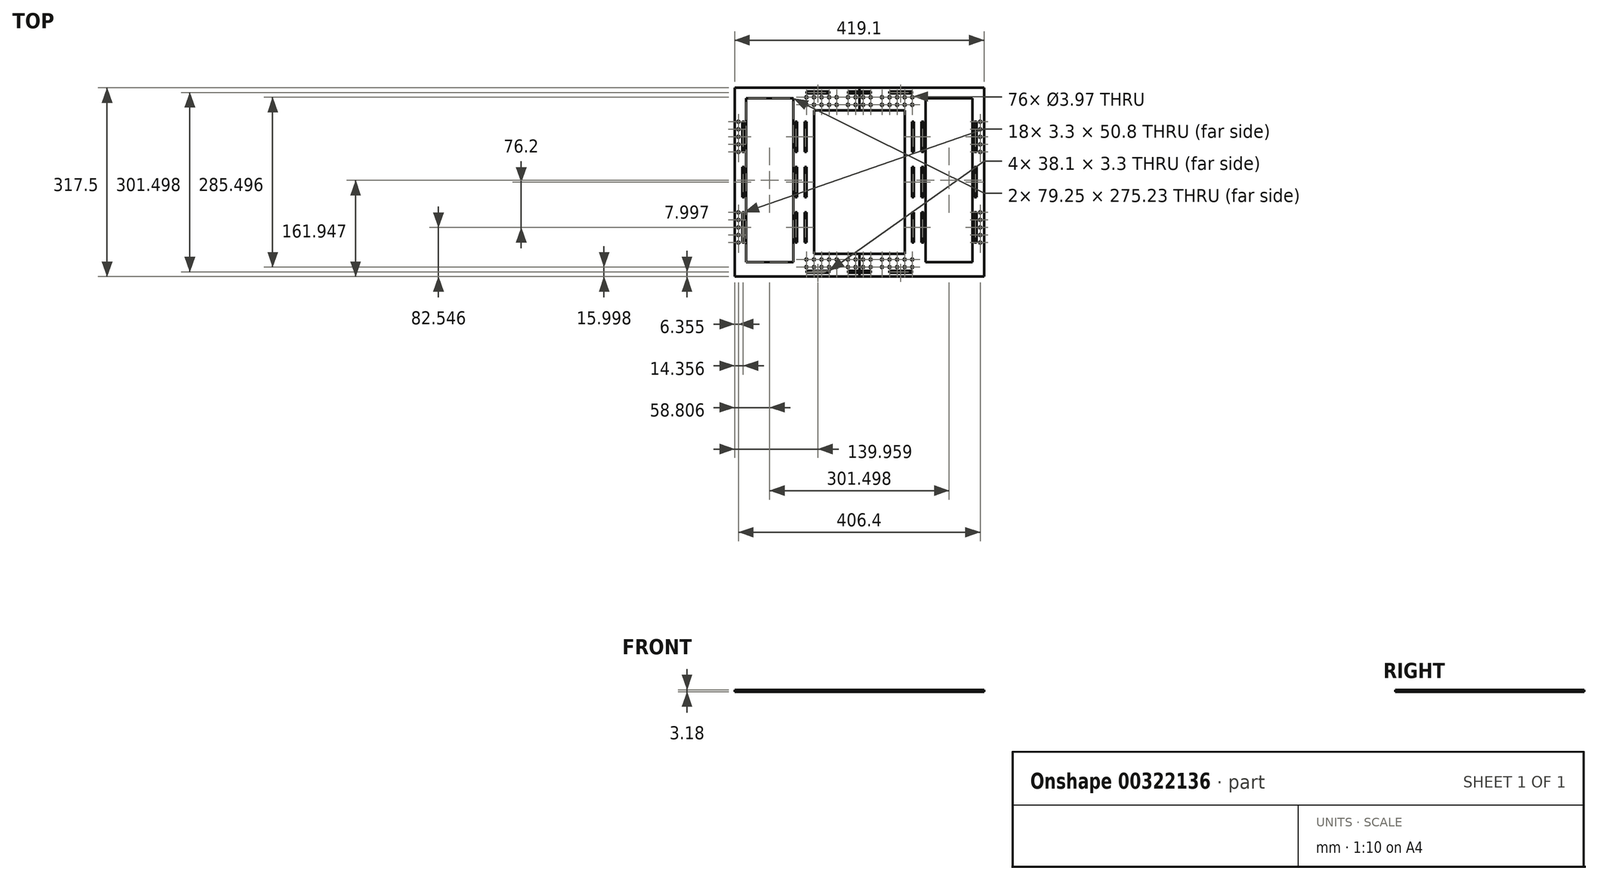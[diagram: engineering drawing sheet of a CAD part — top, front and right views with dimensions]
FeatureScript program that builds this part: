
annotation { "Feature Type Name" : "Feature", "Feature Type Description" : "" }
export const myFeature = defineFeature(function(context is Context, id is Id, definition is map)
    precondition{}
    {
        {
            var Q0;
            Q0=qCreatedBy(makeId("Top.planeOp"),FACE);
            var sketch = newSketch(context, id + "F0", { "sketchPlane" : qUnion([Q0])});
            skCircle(sketch, "E0", {"center": v(-72.78, -151.2) * mm, "radius": 1.98 * mm});
            skCircle(sketch, "E1", {"center": v(-60.08, -151.2) * mm, "radius": 1.98 * mm});
            skCircle(sketch, "E2", {"center": v(-47.38, -151.2) * mm, "radius": 1.98 * mm});
            skCircle(sketch, "E3", {"center": v(-34.68, -151.2) * mm, "radius": 1.98 * mm});
            skCircle(sketch, "E4", {"center": v(-85.48, -151.2) * mm, "radius": 1.98 * mm});
            skCircle(sketch, "E5", {"center": v(41.52, -151.2) * mm, "radius": 1.98 * mm});
            skCircle(sketch, "E6", {"center": v(54.22, -151.2) * mm, "radius": 1.98 * mm});
            skCircle(sketch, "E7", {"center": v(66.92, -151.2) * mm, "radius": 1.98 * mm});
            skCircle(sketch, "E8", {"center": v(79.62, -151.2) * mm, "radius": 1.98 * mm});
            skCircle(sketch, "E9", {"center": v(92.32, -151.2) * mm, "radius": 1.98 * mm});
            skCircle(sketch, "E10.MirrorC", {"center": v(-47.38, 134.3) * mm, "radius": 1.98 * mm});
            skCircle(sketch, "E11.MirrorC", {"center": v(-60.08, 134.3) * mm, "radius": 1.98 * mm});
            skCircle(sketch, "E12.MirrorC", {"center": v(92.32, 134.3) * mm, "radius": 1.98 * mm});
            skCircle(sketch, "E13.MirrorC", {"center": v(-34.68, 134.3) * mm, "radius": 1.98 * mm});
            skCircle(sketch, "E14.MirrorC", {"center": v(-72.78, 134.3) * mm, "radius": 1.98 * mm});
            skCircle(sketch, "E15.MirrorC", {"center": v(-85.48, 134.3) * mm, "radius": 1.98 * mm});
            skCircle(sketch, "E16.MirrorC", {"center": v(54.22, 134.3) * mm, "radius": 1.98 * mm});
            skCircle(sketch, "E17.MirrorC", {"center": v(79.62, 134.3) * mm, "radius": 1.98 * mm});
            skCircle(sketch, "E18.MirrorC", {"center": v(41.52, 134.3) * mm, "radius": 1.98 * mm});
            skCircle(sketch, "E19.MirrorC", {"center": v(66.92, 134.3) * mm, "radius": 1.98 * mm});
            skLineSegment(sketch, "E20.1.0.1", {"start": v(-193.43, 93.16) * mm, "end": v(-193.43, 42.36) * mm});
            skLineSegment(sketch, "E20.1.0.2", {"start": v(-193.43, -59.24) * mm, "end": v(-193.43, -110.04) * mm});
            skLineSegment(sketch, "E20.1.0.4", {"start": v(-193.43, 42.36) * mm, "end": v(-193.43, -33.84) * mm, "construction": true});
            skLineSegment(sketch, "E20.1.0.6", {"start": v(-190.12, -59.24) * mm, "end": v(-190.12, -110.04) * mm});
            skLineSegment(sketch, "E20.1.0.7", {"start": v(-190.12, 16.96) * mm, "end": v(-190.12, -33.84) * mm});
            skLineSegment(sketch, "E20.1.0.9", {"start": v(-186.95, 132.37) * mm, "end": v(-186.95, -142.86) * mm});
            skLineSegment(sketch, "E20.1.0.11", {"start": v(-190.12, 93.16) * mm, "end": v(-190.12, 42.36) * mm});
            skLineSegment(sketch, "E20.1.0.12", {"start": v(-193.43, 16.96) * mm, "end": v(-193.43, -33.84) * mm});
            skLineSegment(sketch, "E20.1.0.14", {"start": v(-193.43, 93.16) * mm, "end": v(-190.12, 93.16) * mm});
            skLineSegment(sketch, "E20.1.0.15", {"start": v(-193.43, -59.24) * mm, "end": v(-190.12, -59.24) * mm});
            skLineSegment(sketch, "E20.1.0.16", {"start": v(-193.43, -110.04) * mm, "end": v(-190.12, -110.04) * mm});
            skLineSegment(sketch, "E20.1.0.17", {"start": v(-193.43, 16.96) * mm, "end": v(-190.12, 16.96) * mm});
            skLineSegment(sketch, "E20.1.0.18", {"start": v(-193.43, 42.36) * mm, "end": v(-190.12, 42.36) * mm});
            skLineSegment(sketch, "E20.1.0.19", {"start": v(-193.43, -33.84) * mm, "end": v(-190.12, -33.84) * mm});
            skLineSegment(sketch, "E21", {"start": v(-206.13, 150.3) * mm, "end": v(-206.13, -167.2) * mm});
            skLineSegment(sketch, "E22.MirrorCS", {"start": v(200.27, -33.84) * mm, "end": v(196.97, -33.84) * mm});
            skLineSegment(sketch, "E23.MirrorCS", {"start": v(200.27, 42.36) * mm, "end": v(196.97, 42.36) * mm});
            skLineSegment(sketch, "E24.MirrorCS", {"start": v(200.27, 93.16) * mm, "end": v(196.97, 93.16) * mm});
            skLineSegment(sketch, "E25.MirrorCS", {"start": v(200.27, -110.04) * mm, "end": v(196.97, -110.04) * mm});
            skLineSegment(sketch, "E26.MirrorCS", {"start": v(200.27, 16.96) * mm, "end": v(196.97, 16.96) * mm});
            skLineSegment(sketch, "E27.MirrorCS", {"start": v(200.27, -59.24) * mm, "end": v(196.97, -59.24) * mm});
            skLineSegment(sketch, "E28.MirrorCS", {"start": v(200.27, 16.96) * mm, "end": v(200.27, -33.84) * mm});
            skLineSegment(sketch, "E29.MirrorCS", {"start": v(200.27, -59.24) * mm, "end": v(200.27, -110.04) * mm});
            skLineSegment(sketch, "E30.MirrorCS", {"start": v(193.8, 132.37) * mm, "end": v(193.8, -142.86) * mm});
            skLineSegment(sketch, "E31.MirrorCS", {"start": v(196.97, -59.24) * mm, "end": v(196.97, -110.04) * mm});
            skLineSegment(sketch, "E32.MirrorCS", {"start": v(200.27, 42.36) * mm, "end": v(200.27, -33.84) * mm, "construction": true});
            skLineSegment(sketch, "E33.MirrorCS", {"start": v(200.27, 93.16) * mm, "end": v(200.27, 42.36) * mm});
            skLineSegment(sketch, "E34.MirrorCS", {"start": v(196.97, 16.96) * mm, "end": v(196.97, -33.84) * mm});
            skLineSegment(sketch, "E35.MirrorCS", {"start": v(196.97, 93.16) * mm, "end": v(196.97, 42.36) * mm});
            skLineSegment(sketch, "E36.MirrorCS", {"start": v(212.97, 150.3) * mm, "end": v(212.97, -167.2) * mm});
            skCircle(sketch, "E37.MirrorC", {"center": v(-199.78, 93.16) * mm, "radius": 1.98 * mm});
            skCircle(sketch, "E38.MirrorC", {"center": v(-199.78, -71.94) * mm, "radius": 1.98 * mm});
            skCircle(sketch, "E39.MirrorC", {"center": v(-199.78, 67.76) * mm, "radius": 1.98 * mm});
            skCircle(sketch, "E40.MirrorC", {"center": v(-199.78, -84.64) * mm, "radius": 1.98 * mm});
            skCircle(sketch, "E41.MirrorC", {"center": v(-199.78, -110.04) * mm, "radius": 1.98 * mm});
            skCircle(sketch, "E42.MirrorC", {"center": v(-199.78, 80.46) * mm, "radius": 1.98 * mm});
            skCircle(sketch, "E43.MirrorC", {"center": v(-199.78, 42.36) * mm, "radius": 1.98 * mm});
            skLineSegment(sketch, "E44.MirrorCS", {"start": v(-193.43, 67.76) * mm, "end": v(-206.13, 67.76) * mm, "construction": true});
            skCircle(sketch, "E45.MirrorC", {"center": v(-199.78, -59.24) * mm, "radius": 1.98 * mm});
            skCircle(sketch, "E46.MirrorC", {"center": v(-199.78, -97.34) * mm, "radius": 1.98 * mm});
            skCircle(sketch, "E47.MirrorC", {"center": v(-199.78, 55.06) * mm, "radius": 1.98 * mm});
            skLineSegment(sketch, "E48.MirrorCS", {"start": v(-190.12, 42.36) * mm, "end": v(-206.13, 42.36) * mm, "construction": true});
            skLineSegment(sketch, "E49.MirrorCS", {"start": v(-193.43, -84.64) * mm, "end": v(-206.13, -84.64) * mm, "construction": true});
            skLineSegment(sketch, "E50.MirrorCS", {"start": v(-199.78, -84.64) * mm, "end": v(-199.78, -110.04) * mm, "construction": true});
            skLineSegment(sketch, "E51.MirrorCS", {"start": v(-199.78, 67.76) * mm, "end": v(-199.78, 93.16) * mm, "construction": true});
            skCircle(sketch, "E52.MirrorC", {"center": v(206.62, -84.64) * mm, "radius": 1.98 * mm});
            skCircle(sketch, "E53.MirrorC", {"center": v(206.62, -71.94) * mm, "radius": 1.98 * mm});
            skCircle(sketch, "E54.MirrorC", {"center": v(206.62, 93.16) * mm, "radius": 1.98 * mm});
            skCircle(sketch, "E55.MirrorC", {"center": v(206.62, 67.76) * mm, "radius": 1.98 * mm});
            skCircle(sketch, "E56.MirrorC", {"center": v(206.62, -110.04) * mm, "radius": 1.98 * mm});
            skCircle(sketch, "E57.MirrorC", {"center": v(206.62, 80.46) * mm, "radius": 1.98 * mm});
            skCircle(sketch, "E58.MirrorC", {"center": v(206.62, 55.06) * mm, "radius": 1.98 * mm});
            skCircle(sketch, "E59.MirrorC", {"center": v(206.62, 42.36) * mm, "radius": 1.98 * mm});
            skCircle(sketch, "E60.MirrorC", {"center": v(206.62, -97.34) * mm, "radius": 1.98 * mm});
            skCircle(sketch, "E61.MirrorC", {"center": v(206.62, -59.24) * mm, "radius": 1.98 * mm});
            skLineSegment(sketch, "E62.MirrorCS", {"start": v(206.62, -84.64) * mm, "end": v(206.62, -110.04) * mm, "construction": true});
            skLineSegment(sketch, "E63.MirrorCS", {"start": v(206.62, 67.76) * mm, "end": v(206.62, 93.16) * mm, "construction": true});
            skLineSegment(sketch, "E64.bottom", {"start": v(114.55, -167.2) * mm, "end": v(-107.7, -167.2) * mm});
            skLineSegment(sketch, "E64.top", {"start": v(114.55, 150.3) * mm, "end": v(-107.7, 150.3) * mm});
            skLineSegment(sketch, "E64.left", {"start": v(114.55, -167.2) * mm, "end": v(114.55, 150.3) * mm, "construction": true});
            skPoint(sketch, "E64.middle", {"position": v(3.42, -8.44) * mm});
            skLineSegment(sketch, "E65.bottom", {"start": v(-85.22, 143.96) * mm, "end": v(-47.12, 143.96) * mm});
            skLineSegment(sketch, "E65.top", {"start": v(-85.22, 140.65) * mm, "end": v(-47.12, 140.65) * mm});
            skLineSegment(sketch, "E65.left", {"start": v(-85.22, 143.96) * mm, "end": v(-85.22, 140.65) * mm});
            skLineSegment(sketch, "E65.right", {"start": v(-47.12, 143.96) * mm, "end": v(-47.12, 140.65) * mm});
            skLineSegment(sketch, "E66.bottom", {"start": v(-15.63, 143.96) * mm, "end": v(22.47, 143.96) * mm});
            skLineSegment(sketch, "E66.top", {"start": v(-15.63, 140.65) * mm, "end": v(22.47, 140.65) * mm});
            skLineSegment(sketch, "E66.left", {"start": v(-15.63, 143.96) * mm, "end": v(-15.63, 140.65) * mm});
            skLineSegment(sketch, "E66.right", {"start": v(22.47, 143.96) * mm, "end": v(22.47, 140.65) * mm});
            skLineSegment(sketch, "E67", {"start": v(-47.12, 143.96) * mm, "end": v(-15.63, 143.96) * mm, "construction": true});
            skLineSegment(sketch, "E68.MirrorCS", {"start": v(92.07, 140.65) * mm, "end": v(53.97, 140.65) * mm});
            skLineSegment(sketch, "E69.MirrorCS", {"start": v(92.07, 143.96) * mm, "end": v(53.97, 143.96) * mm});
            skLineSegment(sketch, "E70.MirrorCS", {"start": v(53.97, 143.96) * mm, "end": v(53.97, 140.65) * mm});
            skLineSegment(sketch, "E71.MirrorCS", {"start": v(92.07, 143.96) * mm, "end": v(92.07, 140.65) * mm});
            skLineSegment(sketch, "E72.MirrorCS", {"start": v(-47.12, -160.84) * mm, "end": v(-47.12, -157.54) * mm});
            skLineSegment(sketch, "E73.MirrorCS", {"start": v(-15.63, -157.54) * mm, "end": v(22.47, -157.54) * mm});
            skLineSegment(sketch, "E74.MirrorCS", {"start": v(22.47, -160.84) * mm, "end": v(22.47, -157.54) * mm});
            skLineSegment(sketch, "E75.MirrorCS", {"start": v(92.07, -157.54) * mm, "end": v(53.97, -157.54) * mm});
            skLineSegment(sketch, "E76.MirrorCS", {"start": v(53.97, -160.84) * mm, "end": v(53.97, -157.54) * mm});
            skLineSegment(sketch, "E77.MirrorCS", {"start": v(-85.22, -157.54) * mm, "end": v(-47.12, -157.54) * mm});
            skLineSegment(sketch, "E78.MirrorCS", {"start": v(92.07, -160.84) * mm, "end": v(92.07, -157.54) * mm});
            skLineSegment(sketch, "E79.MirrorCS", {"start": v(-15.63, -160.84) * mm, "end": v(-15.63, -157.54) * mm});
            skLineSegment(sketch, "E80.MirrorCS", {"start": v(92.07, -160.84) * mm, "end": v(53.97, -160.84) * mm});
            skLineSegment(sketch, "E81.MirrorCS", {"start": v(-15.63, -160.84) * mm, "end": v(22.47, -160.84) * mm});
            skLineSegment(sketch, "E82.MirrorCS", {"start": v(-47.12, -160.84) * mm, "end": v(-15.63, -160.84) * mm, "construction": true});
            skLineSegment(sketch, "E83.MirrorCS", {"start": v(-85.22, -160.84) * mm, "end": v(-47.12, -160.84) * mm});
            skLineSegment(sketch, "E84.MirrorCS", {"start": v(-85.22, -160.84) * mm, "end": v(-85.22, -157.54) * mm});
            skLineSegment(sketch, "E85.bottom", {"start": v(-104.53, 93.16) * mm, "end": v(-101.22, 93.16) * mm});
            skLineSegment(sketch, "E85.top", {"start": v(-104.53, 42.36) * mm, "end": v(-101.22, 42.36) * mm});
            skLineSegment(sketch, "E85.left", {"start": v(-104.53, 93.16) * mm, "end": v(-104.53, 42.36) * mm});
            skLineSegment(sketch, "E85.right", {"start": v(-101.22, 93.16) * mm, "end": v(-101.22, 42.36) * mm});
            skLineSegment(sketch, "E86.0.1.0", {"start": v(-101.22, 16.96) * mm, "end": v(-101.22, -33.84) * mm});
            skLineSegment(sketch, "E86.0.1.1", {"start": v(-104.53, 16.96) * mm, "end": v(-104.53, -33.84) * mm});
            skLineSegment(sketch, "E86.0.1.2", {"start": v(-104.53, 16.96) * mm, "end": v(-101.22, 16.96) * mm});
            skLineSegment(sketch, "E86.0.1.3", {"start": v(-104.53, -33.84) * mm, "end": v(-101.22, -33.84) * mm});
            skLineSegment(sketch, "E86.0.2.0", {"start": v(-101.22, -59.24) * mm, "end": v(-101.22, -110.04) * mm});
            skLineSegment(sketch, "E86.0.2.1", {"start": v(-104.53, -59.24) * mm, "end": v(-104.53, -110.04) * mm});
            skLineSegment(sketch, "E86.0.2.2", {"start": v(-104.53, -59.24) * mm, "end": v(-101.22, -59.24) * mm});
            skLineSegment(sketch, "E86.0.2.3", {"start": v(-104.53, -110.04) * mm, "end": v(-101.22, -110.04) * mm});
            skLineSegment(sketch, "E86.direction1", {"start": v(-104.53, 42.36) * mm, "end": v(-88.52, 42.36) * mm, "construction": true});
            skLineSegment(sketch, "E86.direction2", {"start": v(-104.53, 42.36) * mm, "end": v(-104.53, -33.84) * mm, "construction": true});
            skLineSegment(sketch, "E87.MirrorCS", {"start": v(108.07, 16.96) * mm, "end": v(108.07, -33.84) * mm});
            skLineSegment(sketch, "E88.MirrorCS", {"start": v(111.37, -59.24) * mm, "end": v(108.07, -59.24) * mm});
            skLineSegment(sketch, "E89.MirrorCS", {"start": v(111.37, 16.96) * mm, "end": v(111.37, -33.84) * mm});
            skLineSegment(sketch, "E90.MirrorCS", {"start": v(111.37, -110.04) * mm, "end": v(108.07, -110.04) * mm});
            skLineSegment(sketch, "E91.MirrorCS", {"start": v(111.37, 16.96) * mm, "end": v(108.07, 16.96) * mm});
            skLineSegment(sketch, "E92.MirrorCS", {"start": v(111.37, -33.84) * mm, "end": v(108.07, -33.84) * mm});
            skLineSegment(sketch, "E93.MirrorCS", {"start": v(111.37, 42.36) * mm, "end": v(111.37, -33.84) * mm, "construction": true});
            skLineSegment(sketch, "E94.MirrorCS", {"start": v(111.37, 93.16) * mm, "end": v(108.07, 93.16) * mm});
            skLineSegment(sketch, "E95.MirrorCS", {"start": v(111.37, 42.36) * mm, "end": v(108.07, 42.36) * mm});
            skLineSegment(sketch, "E96.MirrorCS", {"start": v(111.37, 93.16) * mm, "end": v(111.37, 42.36) * mm});
            skLineSegment(sketch, "E97.MirrorCS", {"start": v(108.07, -59.24) * mm, "end": v(108.07, -110.04) * mm});
            skLineSegment(sketch, "E98.MirrorCS", {"start": v(108.07, 93.16) * mm, "end": v(108.07, 42.36) * mm});
            skLineSegment(sketch, "E99.MirrorCS", {"start": v(111.37, -59.24) * mm, "end": v(111.37, -110.04) * mm});
            skLineSegment(sketch, "E100.0.1.0", {"start": v(-85.22, 93.16) * mm, "end": v(-85.22, 42.36) * mm});
            skLineSegment(sketch, "E100.3.1.0", {"start": v(-88.52, 93.16) * mm, "end": v(-88.52, 42.36) * mm});
            skLineSegment(sketch, "E100.6.1.0", {"start": v(-88.52, 93.16) * mm, "end": v(-85.22, 93.16) * mm});
            skLineSegment(sketch, "E100.9.1.0", {"start": v(-88.52, 42.36) * mm, "end": v(-85.22, 42.36) * mm});
            skLineSegment(sketch, "E100.0.1.1", {"start": v(-85.22, 16.96) * mm, "end": v(-85.22, -33.84) * mm});
            skLineSegment(sketch, "E100.3.1.1", {"start": v(-88.52, 16.96) * mm, "end": v(-88.52, -33.84) * mm});
            skLineSegment(sketch, "E100.6.1.1", {"start": v(-88.52, 16.96) * mm, "end": v(-85.22, 16.96) * mm});
            skLineSegment(sketch, "E100.9.1.1", {"start": v(-88.52, -33.84) * mm, "end": v(-85.22, -33.84) * mm});
            skLineSegment(sketch, "E100.0.1.2", {"start": v(-85.22, -59.24) * mm, "end": v(-85.22, -110.04) * mm});
            skLineSegment(sketch, "E100.3.1.2", {"start": v(-88.52, -59.24) * mm, "end": v(-88.52, -110.04) * mm});
            skLineSegment(sketch, "E100.6.1.2", {"start": v(-88.52, -59.24) * mm, "end": v(-85.22, -59.24) * mm});
            skLineSegment(sketch, "E100.9.1.2", {"start": v(-88.52, -110.04) * mm, "end": v(-85.22, -110.04) * mm});
            skLineSegment(sketch, "E101.MirrorCS", {"start": v(95.37, 93.16) * mm, "end": v(95.37, 42.36) * mm});
            skLineSegment(sketch, "E102.MirrorCS", {"start": v(95.37, 93.16) * mm, "end": v(92.07, 93.16) * mm});
            skLineSegment(sketch, "E103.MirrorCS", {"start": v(95.37, 42.36) * mm, "end": v(92.07, 42.36) * mm});
            skLineSegment(sketch, "E104.MirrorCS", {"start": v(95.37, -59.24) * mm, "end": v(95.37, -110.04) * mm});
            skLineSegment(sketch, "E105.MirrorCS", {"start": v(92.07, 16.96) * mm, "end": v(92.07, -33.84) * mm});
            skLineSegment(sketch, "E106.MirrorCS", {"start": v(95.37, -59.24) * mm, "end": v(92.07, -59.24) * mm});
            skLineSegment(sketch, "E107.MirrorCS", {"start": v(95.37, 16.96) * mm, "end": v(95.37, -33.84) * mm});
            skLineSegment(sketch, "E108.MirrorCS", {"start": v(95.37, -110.04) * mm, "end": v(92.07, -110.04) * mm});
            skLineSegment(sketch, "E109.MirrorCS", {"start": v(95.37, 16.96) * mm, "end": v(92.07, 16.96) * mm});
            skLineSegment(sketch, "E110.MirrorCS", {"start": v(95.37, -33.84) * mm, "end": v(92.07, -33.84) * mm});
            skLineSegment(sketch, "E111.MirrorCS", {"start": v(92.07, 93.16) * mm, "end": v(92.07, 42.36) * mm});
            skLineSegment(sketch, "E112.MirrorCS", {"start": v(92.07, -59.24) * mm, "end": v(92.07, -110.04) * mm});
            skLineSegment(sketch, "E113", {"start": v(-85.22, 93.16) * mm, "end": v(-85.22, 140.65) * mm, "construction": true});
            skLineSegment(sketch, "E114", {"start": v(114.55, 150.3) * mm, "end": v(212.97, 150.3) * mm});
            skLineSegment(sketch, "E115", {"start": v(212.97, -167.2) * mm, "end": v(114.55, -167.2) * mm});
            skLineSegment(sketch, "E116.bottom", {"start": v(114.55, 132.37) * mm, "end": v(193.8, 132.37) * mm});
            skLineSegment(sketch, "E116.top", {"start": v(114.55, -142.86) * mm, "end": v(193.8, -142.86) * mm});
            skLineSegment(sketch, "E116.left", {"start": v(114.55, 132.37) * mm, "end": v(114.55, -142.86) * mm});
            skLineSegment(sketch, "E117.MirrorCS", {"start": v(-107.7, -167.2) * mm, "end": v(-107.7, 150.3) * mm, "construction": true});
            skLineSegment(sketch, "E118.MirrorCS", {"start": v(-107.7, 150.3) * mm, "end": v(-206.13, 150.3) * mm});
            skLineSegment(sketch, "E119.MirrorCS", {"start": v(-206.13, -167.2) * mm, "end": v(-107.7, -167.2) * mm});
            skLineSegment(sketch, "E120.MirrorCS", {"start": v(-107.7, -142.86) * mm, "end": v(-186.95, -142.86) * mm});
            skLineSegment(sketch, "E121.MirrorCS", {"start": v(-107.7, 132.37) * mm, "end": v(-186.95, 132.37) * mm});
            skLineSegment(sketch, "E122", {"start": v(-107.7, 132.37) * mm, "end": v(-107.7, -142.86) * mm});
            skPoint(sketch, "E123", {"position": v(3.42, 140.65) * mm});
            skLineSegment(sketch, "E124.bottom", {"start": v(79.62, -129.1) * mm, "end": v(-72.78, -129.1) * mm});
            skLineSegment(sketch, "E124.top", {"start": v(79.62, 112.2) * mm, "end": v(-72.78, 112.2) * mm});
            skLineSegment(sketch, "E124.left", {"start": v(79.62, -129.1) * mm, "end": v(79.62, 112.2) * mm});
            skLineSegment(sketch, "E124.right", {"start": v(-72.78, -129.1) * mm, "end": v(-72.78, 112.2) * mm});
            skLineSegment(sketch, "E125", {"start": v(3.42, -8.44) * mm, "end": v(3.42, 150.3) * mm});
            skLineSegment(sketch, "E126", {"start": v(3.42, -8.44) * mm, "end": v(3.42, -167.2) * mm});
            skCircle(sketch, "E127.0.1.0", {"center": v(-34.68, 121.6) * mm, "radius": 1.98 * mm});
            skCircle(sketch, "E127.0.1.1", {"center": v(-72.78, 121.6) * mm, "radius": 1.98 * mm});
            skCircle(sketch, "E127.0.1.2", {"center": v(-85.48, 121.6) * mm, "radius": 1.98 * mm});
            skCircle(sketch, "E127.0.1.3", {"center": v(-47.38, 121.6) * mm, "radius": 1.98 * mm});
            skCircle(sketch, "E127.0.1.4", {"center": v(-60.08, 121.6) * mm, "radius": 1.98 * mm});
            skLineSegment(sketch, "E127.direction1", {"start": v(-85.48, 134.3) * mm, "end": v(-60.08, 134.3) * mm, "construction": true});
            skLineSegment(sketch, "E127.direction2", {"start": v(-85.48, 134.3) * mm, "end": v(-85.48, 121.6) * mm, "construction": true});
            skCircle(sketch, "E128.MirrorC", {"center": v(66.92, 121.6) * mm, "radius": 1.98 * mm});
            skLineSegment(sketch, "E129.MirrorCS", {"start": v(92.32, 134.3) * mm, "end": v(92.32, 121.6) * mm, "construction": true});
            skLineSegment(sketch, "E130.MirrorCS", {"start": v(92.07, 93.16) * mm, "end": v(92.07, 140.65) * mm, "construction": true});
            skCircle(sketch, "E131.MirrorC", {"center": v(41.52, 121.6) * mm, "radius": 1.98 * mm});
            skCircle(sketch, "E132.MirrorC", {"center": v(79.62, 121.6) * mm, "radius": 1.98 * mm});
            skCircle(sketch, "E133.MirrorC", {"center": v(92.32, 121.6) * mm, "radius": 1.98 * mm});
            skCircle(sketch, "E134.MirrorC", {"center": v(54.22, 121.6) * mm, "radius": 1.98 * mm});
            skLineSegment(sketch, "E135", {"start": v(-17.57, -8.44) * mm, "end": v(22.05, -8.44) * mm});
            skCircle(sketch, "E136.MirrorC", {"center": v(-85.48, -138.5) * mm, "radius": 1.98 * mm});
            skCircle(sketch, "E137.MirrorC", {"center": v(92.32, -138.5) * mm, "radius": 1.98 * mm});
            skCircle(sketch, "E138.MirrorC", {"center": v(-72.78, -138.5) * mm, "radius": 1.98 * mm});
            skCircle(sketch, "E139.MirrorC", {"center": v(-34.68, -138.5) * mm, "radius": 1.98 * mm});
            skCircle(sketch, "E140.MirrorC", {"center": v(54.22, -138.5) * mm, "radius": 1.98 * mm});
            skCircle(sketch, "E141.MirrorC", {"center": v(79.62, -138.5) * mm, "radius": 1.98 * mm});
            skCircle(sketch, "E142.MirrorC", {"center": v(41.52, -138.5) * mm, "radius": 1.98 * mm});
            skCircle(sketch, "E143.MirrorC", {"center": v(66.92, -138.5) * mm, "radius": 1.98 * mm});
            skCircle(sketch, "E144.MirrorC", {"center": v(-60.08, -138.5) * mm, "radius": 1.98 * mm});
            skCircle(sketch, "E145.MirrorC", {"center": v(-47.38, -138.5) * mm, "radius": 1.98 * mm});
            skCircle(sketch, "E146", {"center": v(-15.63, 134.3) * mm, "radius": 1.98 * mm});
            skCircle(sketch, "E147.0.1.0", {"center": v(-15.63, 121.6) * mm, "radius": 1.98 * mm});
            skCircle(sketch, "E147.1.0.0", {"center": v(-2.93, 134.3) * mm, "radius": 1.98 * mm});
            skCircle(sketch, "E147.1.1.0", {"center": v(-2.93, 121.6) * mm, "radius": 1.98 * mm});
            skCircle(sketch, "E147.2.0.0", {"center": v(9.77, 134.3) * mm, "radius": 1.98 * mm});
            skCircle(sketch, "E147.2.1.0", {"center": v(9.77, 121.6) * mm, "radius": 1.98 * mm});
            skCircle(sketch, "E147.3.0.0", {"center": v(22.47, 134.3) * mm, "radius": 1.98 * mm});
            skCircle(sketch, "E147.3.1.0", {"center": v(22.47, 121.6) * mm, "radius": 1.98 * mm});
            skLineSegment(sketch, "E147.direction1", {"start": v(-15.63, 134.3) * mm, "end": v(-2.93, 134.3) * mm, "construction": true});
            skLineSegment(sketch, "E147.direction2", {"start": v(-15.63, 134.3) * mm, "end": v(-15.63, 121.6) * mm, "construction": true});
            skCircle(sketch, "E148.MirrorC", {"center": v(-2.93, -138.5) * mm, "radius": 1.98 * mm});
            skCircle(sketch, "E149.MirrorC", {"center": v(9.77, -151.2) * mm, "radius": 1.98 * mm});
            skCircle(sketch, "E150.MirrorC", {"center": v(-15.63, -151.2) * mm, "radius": 1.98 * mm});
            skLineSegment(sketch, "E151.MirrorCS", {"start": v(-15.63, -151.2) * mm, "end": v(-2.93, -151.2) * mm, "construction": true});
            skCircle(sketch, "E152.MirrorC", {"center": v(9.77, -138.5) * mm, "radius": 1.98 * mm});
            skCircle(sketch, "E153.MirrorC", {"center": v(-15.63, -138.5) * mm, "radius": 1.98 * mm});
            skLineSegment(sketch, "E154.MirrorCS", {"start": v(-15.63, -151.2) * mm, "end": v(-15.63, -138.5) * mm, "construction": true});
            skCircle(sketch, "E155.MirrorC", {"center": v(22.47, -151.2) * mm, "radius": 1.98 * mm});
            skCircle(sketch, "E156.MirrorC", {"center": v(-2.93, -151.2) * mm, "radius": 1.98 * mm});
            skCircle(sketch, "E157.MirrorC", {"center": v(22.47, -138.5) * mm, "radius": 1.98 * mm});
            skSolve(sketch);
        }
        {
            var Q0;
            Q0=makeQuery(id+"F0.imprint","IMPRINT",FACE,{"disambiguationData":[TD([[makeQuery(id+"F0.imprint","IMPRINT",EDGE,{"derivedFrom":sQuery(id+"F0.wireOp",EDGE,"E0")}),-1.0]])]});
            extrude(context, id + "F1", {"entities" : qUnion([Q0]), "depth" : 3.17 * mm});
        }
        {
            var Q0;
            Q0=makeQuery(id+"F0.imprint","IMPRINT",FACE,{"disambiguationData":[TD([[makeQuery(id+"F0.imprint","IMPRINT",EDGE,{"derivedFrom":sQuery(id+"F0.wireOp",EDGE,"E5")}),-1.0]])]});
            extrude(context, id + "F2", {"entities" : qUnion([Q0]), "depth" : 3.17 * mm});
        }
    });
